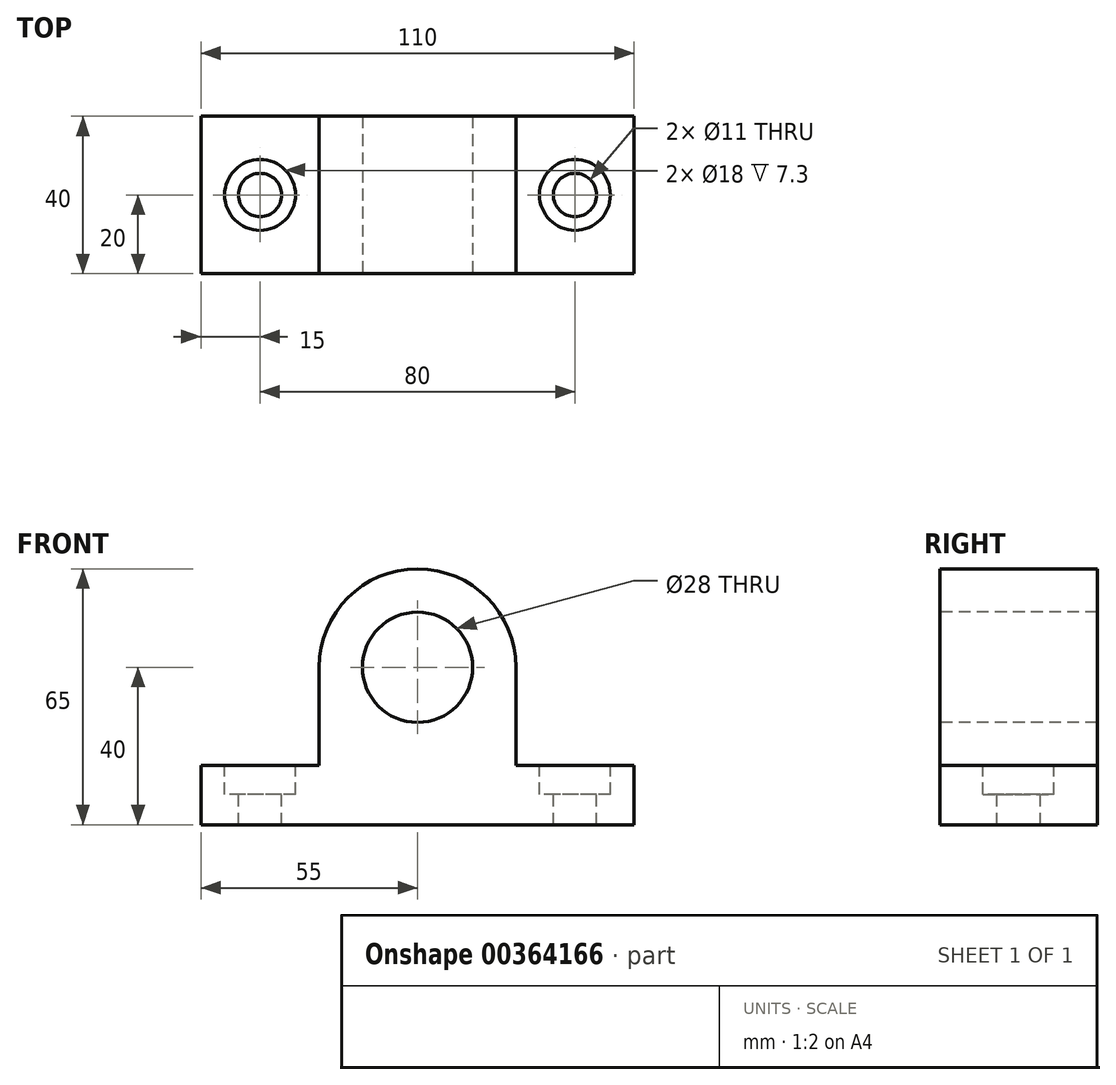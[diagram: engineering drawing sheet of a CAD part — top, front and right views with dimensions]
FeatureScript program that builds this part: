
annotation { "Feature Type Name" : "Feature", "Feature Type Description" : "" }
export const myFeature = defineFeature(function(context is Context, id is Id, definition is map)
    precondition{}
    {
        {
            var Q0;
            Q0=qCreatedBy(makeId("Top.planeOp"),FACE);
            var sketch = newSketch(context, id + "F0", { "sketchPlane" : qUnion([Q0])});
            skLineSegment(sketch, "E0.bottom", {"start": v(-55, -20) * mm, "end": v(55, -20) * mm});
            skLineSegment(sketch, "E0.top", {"start": v(-55, 20) * mm, "end": v(55, 20) * mm});
            skLineSegment(sketch, "E0.left", {"start": v(-55, -20) * mm, "end": v(-55, 20) * mm});
            skLineSegment(sketch, "E0.right", {"start": v(55, -20) * mm, "end": v(55, 20) * mm});
            skPoint(sketch, "E0.middle", {"position": v(0, 0) * mm});
            skSolve(sketch);
        }
        {
            var Q0;
            Q0=makeQuery(id+"F0.imprint","IMPRINT",FACE,{"disambiguationData":[TD([[makeQuery(id+"F0.imprint","IMPRINT",EDGE,{"derivedFrom":sQuery(id+"F0.wireOp",EDGE,"E0.bottom")}),1.0]])]});
            extrude(context, id + "F1", {"entities" : qUnion([Q0]), "depth" : 65 * mm});
        }
        {
            var Q0;
            Q0=makeQuery(id+"F1.opExtrude","CAP_FACE",FACE,{"disambiguationData":[OSD([sQuery(id+"F0.wireOp",EDGE,"E0.bottom"),sQuery(id+"F0.wireOp",EDGE,"E0.top"),sQuery(id+"F0.wireOp",EDGE,"E0.left"),sQuery(id+"F0.wireOp",EDGE,"E0.right")])],"isStart":false});
            var sketch = newSketch(context, id + "F2", { "sketchPlane" : qUnion([Q0])});
            skCircle(sketch, "E1", {"center": v(-40, 0) * mm, "radius": 5.5 * mm});
            skPoint(sketch, "E1.centerSnap0", {"position": v(-55, 0) * mm});
            skCircle(sketch, "E2", {"center": v(40, 0) * mm, "radius": 5.5 * mm});
            skCircle(sketch, "E3", {"center": v(-40, 0) * mm, "radius": 9 * mm});
            skCircle(sketch, "E4", {"center": v(40, 0) * mm, "radius": 9 * mm});
            skSolve(sketch);
        }
        {
            var Q0;
            Q0=makeQuery(id+"F2.imprint","IMPRINT",FACE,{"disambiguationData":[TD([[makeQuery(id+"F2.imprint","IMPRINT",EDGE,{"derivedFrom":sQuery(id+"F2.wireOp",EDGE,"E1")}),1.0]])]});
            var Q1;
            Q1=makeQuery(id+"F2.imprint","IMPRINT",FACE,{"disambiguationData":[TD([[makeQuery(id+"F2.imprint","IMPRINT",EDGE,{"derivedFrom":sQuery(id+"F2.wireOp",EDGE,"E2")}),1.0]])]});
            extrude(context, id + "F3", {"entities" : qUnion([Q0, Q1]), "operationType" : NewBodyOperationType.REMOVE, "oppositeDirection" : true, "depth" : 80 * mm});
        }
        {
            var Q0;
            Q0=qSketchRegion(id+"F2",true);
            extrude(context, id + "F4", {"entities" : qUnion([Q0]), "operationType" : NewBodyOperationType.REMOVE, "oppositeDirection" : true, "depth" : 57.3 * mm});
        }
        {
            var Q0;
            Q0=makeQuery(id+"F1.opExtrude","SWEPT_FACE",FACE,{"disambiguationData":[OSD([sQuery(id+"F0.wireOp",EDGE,"E0.bottom")])]});
            var sketch = newSketch(context, id + "F5", { "sketchPlane" : qUnion([Q0])});
            skLineSegment(sketch, "E5", {"start": v(-55, 15) * mm, "end": v(-25, 15) * mm});
            skLineSegment(sketch, "E6", {"start": v(-25, 15) * mm, "end": v(-25, 44.02) * mm});
            skLineSegment(sketch, "E7", {"start": v(25, 44.02) * mm, "end": v(25, 15) * mm});
            skLineSegment(sketch, "E8", {"start": v(25, 15) * mm, "end": v(55, 15) * mm});
            skCircle(sketch, "E9", {"center": v(0, 40) * mm, "radius": 25 * mm});
            skCircle(sketch, "E10", {"center": v(0, 40) * mm, "radius": 14 * mm});
            skSolve(sketch);
        }
        {
            var Q0;
            Q0=makeQuery(id+"F5.imprint","IMPRINT",FACE,{"disambiguationData":[TD([[makeQuery(id+"F5.imprint","IMPRINT",EDGE,{"derivedFrom":sQuery(id+"F5.wireOp",EDGE,"E10")}),1.0]])]});
            var Q1;
            {var subQ1=sQuery(id+"F5.wireOp",EDGE,"E5");Q1=makeQuery(id+"F5.imprint","IMPRINT",FACE,{"disambiguationData":[TD([[makeQuery(id+"F5.imprint","IMPRINT",EDGE,{"derivedFrom":subQ1}),1.0]])]});}
            var Q2;
            {var subQ6=sQuery(id+"F5.wireOp",EDGE,"E8");Q2=makeQuery(id+"F5.imprint","IMPRINT",FACE,{"disambiguationData":[TD([[makeQuery(id+"F5.imprint","IMPRINT",EDGE,{"derivedFrom":subQ6}),1.0]])]});}
            extrude(context, id + "F6", {"entities" : qUnion([Q0, Q1, Q2]), "operationType" : NewBodyOperationType.REMOVE, "oppositeDirection" : true, "depth" : 80 * mm});
        }
    });
